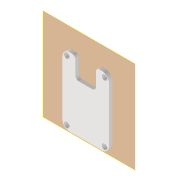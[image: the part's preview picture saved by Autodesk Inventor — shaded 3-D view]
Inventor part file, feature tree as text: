
AUTODESK INVENTOR PART (.ipt)
format: ipt  version: 2022 (Build 260153000, 153)  size: 176,128 bytes
history: native  units: mm
features: reference x5, other x4, extrude x3, plane x2, sketch x2, hole x1, fillet x1, projected_geometry x1
ambient origin geometry x8: Origin, YZ Plane, XZ Plane, XY Plane, X Axis, Y Axis, Z Axis, Center Point
bodies: Volumenkörper1 (feature_tree)
feature tree (19):
  plane  "Arbeitsebene1"
  extrude  "Extrusion1"  Depth=10.0mm
  plane  "Arbeitsebene2"
  hole  "Bohrung1"  [1 undecoded]
  extrude  "Extrusion2"  Depth=10.0mm
  fillet  "Rundung2"  Radius=3.0mm
  extrude  "Extrusion3"  Depth=4.0mm
  reference  "Referenz9"
  reference  "Referenz10"
  projected_geometry  "Projizierte Kontur3"
  sketch  "Skizze4"  dims[d2=2.0mm d3=0.0mm]
  reference  "Referenz11"
  reference  "Referenz12"
  sketch  "Skizze5"  dims[d4=3.2mm d5=6.0mm d6=4.0mm d7=2.0mm d8=90.0deg d9=8.0mm d10=20.594885mm d21=2.5mm d22=0.5mm d23=0.5mm d24=3.0mm d25=0.0mm d26=4.0mm d27=10.0mm d28=0.0mm]
  reference  "Referenz13"
  other  "Assembly_Cube_SEEED_Xiao_Sense_Camera_adapter_v3.iam"
  other  "00_ESP32_XIAO_Adapter_base:1"
  other  "Assembly_Cube_SEEED_Xiao_Sense_Camera_v3.iam"
  other  "20_Cube_Insert_SEEED_Xiao_Sense_Camera:1"
note: 1 required parameter value undecoded (feature->parameter linkage not recoverable at this tier; creation-order binding heuristic only, values carry confidence <= 0.55)
